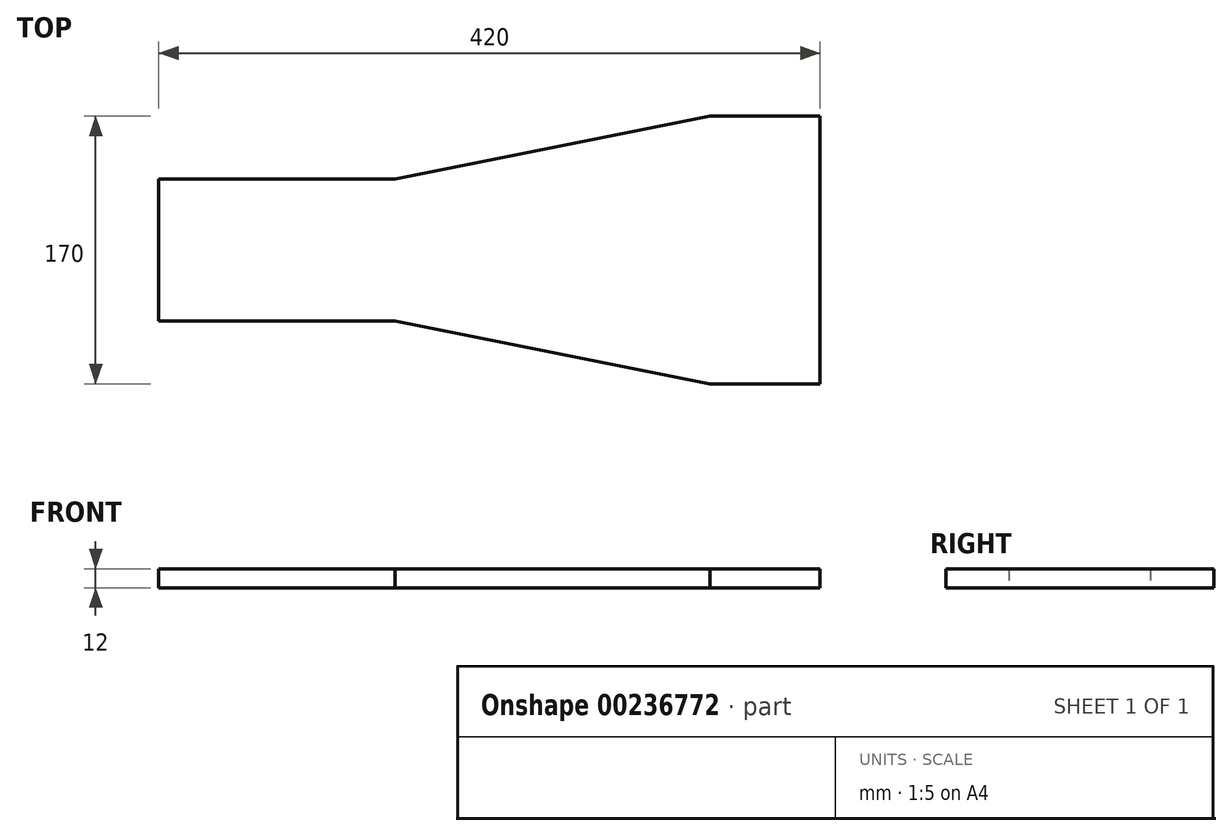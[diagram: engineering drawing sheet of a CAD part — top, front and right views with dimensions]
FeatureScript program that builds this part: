
annotation { "Feature Type Name" : "Feature", "Feature Type Description" : "" }
export const myFeature = defineFeature(function(context is Context, id is Id, definition is map)
    precondition{}
    {
        {
            var Q0;
            Q0=qCreatedBy(makeId("Top.planeOp"),FACE);
            var sketch = newSketch(context, id + "F0", { "sketchPlane" : qUnion([Q0])});
            skLineSegment(sketch, "E0.bottom", {"start": v(210, 85) * mm, "end": v(140, 85) * mm});
            skLineSegment(sketch, "E0.top", {"start": v(210, -85) * mm, "end": v(140, -85) * mm});
            skLineSegment(sketch, "E0.left", {"start": v(210, 85) * mm, "end": v(210, -85) * mm});
            skLineSegment(sketch, "E0.right", {"start": v(-210, 45) * mm, "end": v(-210, -45) * mm});
            skPoint(sketch, "E0.middle", {"position": v(0, 0) * mm});
            skLineSegment(sketch, "E1", {"start": v(-210, 45) * mm, "end": v(-60, 45) * mm});
            skLineSegment(sketch, "E2", {"start": v(-60, 45) * mm, "end": v(140, 85) * mm});
            skLineSegment(sketch, "E3", {"start": v(-210, -45) * mm, "end": v(-60, -45) * mm});
            skLineSegment(sketch, "E4", {"start": v(-60, -45) * mm, "end": v(140, -85) * mm});
            skPoint(sketch, "E5.orphan", {"position": v(-210, 85) * mm});
            skPoint(sketch, "E6.orphan", {"position": v(-210, -85) * mm});
            skSolve(sketch);
        }
        {
            var Q0;
            Q0 = qSketchRegion(id + "F0", true);
            extrude(context, id + "F1", {"entities" : qUnion([Q0]), "depth" : 12 * mm, "offsetDistance" : 25 * mm});
        }
    });
